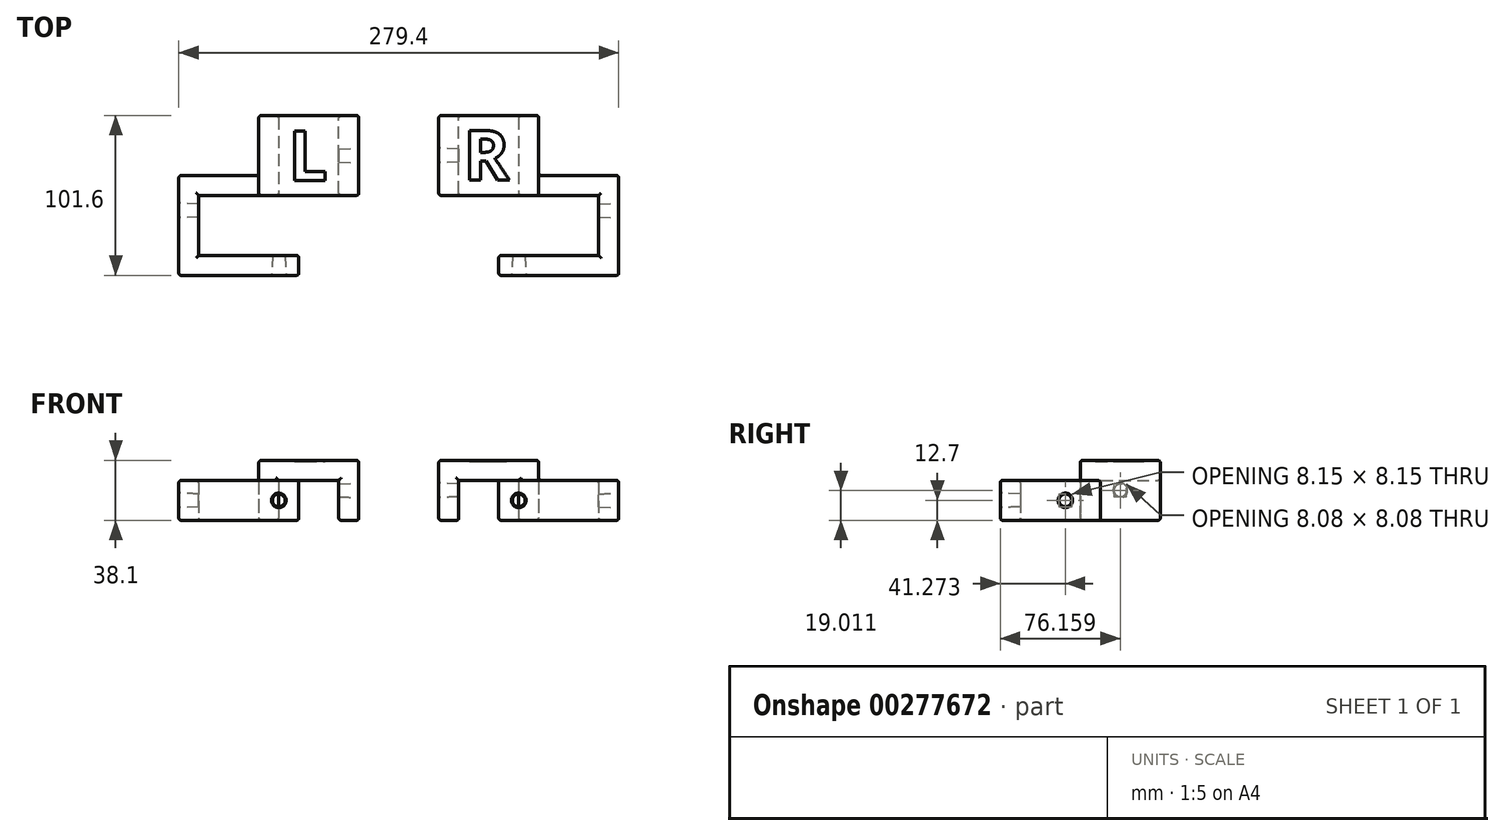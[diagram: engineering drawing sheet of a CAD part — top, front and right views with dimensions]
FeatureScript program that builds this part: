
annotation { "Feature Type Name" : "Feature", "Feature Type Description" : "" }
export const myFeature = defineFeature(function(context is Context, id is Id, definition is map)
    precondition{}
    {
        {
            var Q0;
            Q0=qCreatedBy(makeId("Top.planeOp"),FACE);
            var sketch = newSketch(context, id + "F0", { "sketchPlane" : qUnion([Q0])});
            skLineSegment(sketch, "E0.bottom", {"start": v(0.5, -16.27) * mm, "end": v(-75.7, -16.27) * mm});
            skLineSegment(sketch, "E0.top", {"start": v(0.5, -3.57) * mm, "end": v(-63, -3.57) * mm});
            skLineSegment(sketch, "E0.left", {"start": v(0.5, -16.27) * mm, "end": v(0.5, -3.57) * mm});
            skLineSegment(sketch, "E1", {"start": v(-75.7, -16.27) * mm, "end": v(-75.7, 47.23) * mm});
            skLineSegment(sketch, "E2", {"start": v(-75.7, 47.23) * mm, "end": v(-24.9, 47.23) * mm});
            skLineSegment(sketch, "E3", {"start": v(-24.9, 47.23) * mm, "end": v(-24.9, 85.33) * mm});
            skLineSegment(sketch, "E4", {"start": v(-24.9, 85.33) * mm, "end": v(-12.2, 85.33) * mm});
            skLineSegment(sketch, "E5", {"start": v(-12.2, 85.33) * mm, "end": v(-12.2, 34.53) * mm});
            skLineSegment(sketch, "E6", {"start": v(-12.2, 34.53) * mm, "end": v(-63, 34.53) * mm});
            skLineSegment(sketch, "E7", {"start": v(-63, 34.53) * mm, "end": v(-63, -3.57) * mm});
            skSolve(sketch);
        }
        {
            var Q0;
            Q0 = qSketchRegion(id + "F0", true);
            extrude(context, id + "F1", {"entities" : qUnion([Q0]), "depth" : 25.4 * mm});
        }
        {
            var Q0;
            Q0=makeQuery(id+"F1.opExtrude","CAP_FACE",FACE,{"disambiguationData":[OSD([sQuery(id+"F0.wireOp",EDGE,"E0.bottom"),sQuery(id+"F0.wireOp",EDGE,"E0.top"),sQuery(id+"F0.wireOp",EDGE,"E0.left"),sQuery(id+"F0.wireOp",EDGE,"E1"),sQuery(id+"F0.wireOp",EDGE,"E2"),sQuery(id+"F0.wireOp",EDGE,"E3"),sQuery(id+"F0.wireOp",EDGE,"E4"),sQuery(id+"F0.wireOp",EDGE,"E5"),sQuery(id+"F0.wireOp",EDGE,"E6"),sQuery(id+"F0.wireOp",EDGE,"E7")])],"isStart":false});
            var sketch = newSketch(context, id + "F2", { "sketchPlane" : qUnion([Q0])});
            skLineSegment(sketch, "E8.bottom", {"start": v(-24.9, 85.33) * mm, "end": v(38.6, 85.33) * mm});
            skLineSegment(sketch, "E8.top", {"start": v(-24.9, 34.53) * mm, "end": v(38.6, 34.53) * mm});
            skLineSegment(sketch, "E8.left", {"start": v(-24.9, 85.33) * mm, "end": v(-24.9, 34.53) * mm});
            skLineSegment(sketch, "E8.right", {"start": v(38.6, 85.33) * mm, "end": v(38.6, 34.53) * mm});
            skSolve(sketch);
        }
        {
            var Q0;
            Q0 = qSketchRegion(id + "F2", true);
            extrude(context, id + "F3", {"entities" : qUnion([Q0]), "operationType" : NewBodyOperationType.ADD, "depth" : 12.7 * mm});
        }
        {
            var Q0;
            Q0=makeQuery(id+"F3.opExtrude","CAP_FACE",FACE,{"disambiguationData":[OSD([sQuery(id+"F2.wireOp",EDGE,"E8.bottom"),sQuery(id+"F2.wireOp",EDGE,"E8.top"),sQuery(id+"F2.wireOp",EDGE,"E8.left"),sQuery(id+"F2.wireOp",EDGE,"E8.right")])],"isStart":true});
            var sketch = newSketch(context, id + "F4", { "sketchPlane" : qUnion([Q0])});
            skLineSegment(sketch, "E9.bottom", {"start": v(38.6, -34.53) * mm, "end": v(25.9, -34.53) * mm});
            skLineSegment(sketch, "E9.top", {"start": v(38.6, -85.33) * mm, "end": v(25.9, -85.33) * mm});
            skLineSegment(sketch, "E9.left", {"start": v(38.6, -34.53) * mm, "end": v(38.6, -85.33) * mm});
            skLineSegment(sketch, "E9.right", {"start": v(25.9, -34.53) * mm, "end": v(25.9, -85.33) * mm});
            skSolve(sketch);
        }
        {
            var Q0;
            Q0 = qSketchRegion(id + "F4", true);
            extrude(context, id + "F5", {"entities" : qUnion([Q0]), "operationType" : NewBodyOperationType.ADD, "depth" : 25.4 * mm});
        }
        {
            var Q0;
            Q0=makeQuery(id+"F1.opExtrude","SWEPT_FACE",FACE,{"disambiguationData":[OSD([sQuery(id+"F0.wireOp",EDGE,"E0.bottom")])]});
            var sketch = newSketch(context, id + "F6", { "sketchPlane" : qUnion([Q0])});
            skLineSegment(sketch, "E10", {"start": v(0.5, 12.7) * mm, "end": v(-12.2, 12.7) * mm, "construction": true});
            skCircle(sketch, "E11", {"center": v(-12.2, 12.7) * mm, "radius": 4.61 * mm});
            skSolve(sketch);
        }
        {
            var Q0;
            Q0=makeQuery(id+"F1.opExtrude","SWEPT_FACE",FACE,{"disambiguationData":[OSD([sQuery(id+"F0.wireOp",EDGE,"E0.top")])]});
            var sketch = newSketch(context, id + "F7", { "sketchPlane" : qUnion([Q0])});
            skPoint(sketch, "E12.0", {"position": v(12.2, 12.7) * mm});
            skCircle(sketch, "E13", {"center": v(12.2, 12.7) * mm, "radius": 4.08 * mm});
            skSolve(sketch);
        }
        {
            var Q0;
            Q0=makeQuery(id+"F1.opExtrude","SWEPT_FACE",FACE,{"disambiguationData":[OSD([sQuery(id+"F0.wireOp",EDGE,"E1")])]});
            var sketch = newSketch(context, id + "F8", { "sketchPlane" : qUnion([Q0])});
            skLineSegment(sketch, "E14", {"start": v(-47.23, 12.7) * mm, "end": v(-25, 12.7) * mm, "construction": true});
            skCircle(sketch, "E15", {"center": v(-25, 12.7) * mm, "radius": 4.61 * mm});
            skSolve(sketch);
        }
        {
            var Q0;
            Q0=makeQuery(id+"F1.opExtrude","SWEPT_FACE",FACE,{"disambiguationData":[OSD([sQuery(id+"F0.wireOp",EDGE,"E7")])]});
            var sketch = newSketch(context, id + "F9", { "sketchPlane" : qUnion([Q0])});
            skPoint(sketch, "E16.0", {"position": v(25, 12.7) * mm});
            skCircle(sketch, "E17", {"center": v(25, 12.7) * mm, "radius": 4.08 * mm});
            skSolve(sketch);
        }
        {
            var Q0;
            Q0=makeQuery(id+"F5.boolean.opBoolean","MERGE",FACE,{"derivedFrom":[makeQuery(id+"F3.opExtrude","SWEPT_FACE",FACE,{"disambiguationData":[OSD([sQuery(id+"F2.wireOp",EDGE,"E8.right")])]}),makeQuery(id+"F5.opExtrude","SWEPT_FACE",FACE,{"disambiguationData":[OSD([sQuery(id+"F4.wireOp",EDGE,"E9.left")])]})]});
            var sketch = newSketch(context, id + "F10", { "sketchPlane" : qUnion([Q0])});
            skLineSegment(sketch, "E18", {"start": v(34.53, 19.05) * mm, "end": v(59.93, 19.05) * mm, "construction": true});
            skLineSegment(sketch, "E19", {"start": v(59.93, 19.05) * mm, "end": v(59.93, 0) * mm, "construction": true});
            skCircle(sketch, "E20", {"center": v(59.93, 19.05) * mm, "radius": 4.61 * mm});
            skSolve(sketch);
        }
        {
            var Q0;
            Q0=makeQuery(id+"F5.opExtrude","SWEPT_FACE",FACE,{"disambiguationData":[OSD([sQuery(id+"F4.wireOp",EDGE,"E9.right")])]});
            var sketch = newSketch(context, id + "F11", { "sketchPlane" : qUnion([Q0])});
            skPoint(sketch, "E21.0", {"position": v(-59.93, 19.05) * mm});
            skCircle(sketch, "E22", {"center": v(-59.93, 19.05) * mm, "radius": 4.08 * mm});
            skSolve(sketch);
        }
        {
            var Q1;
            Q1=makeQuery(id+"F10.imprint","IMPRINT",FACE,{"disambiguationData":[TD([[makeQuery(id+"F10.imprint","IMPRINT",EDGE,{"derivedFrom":sQuery(id+"F10.wireOp",EDGE,"E20")}),1.0]])]});
            var Q2;
            Q2=makeQuery(id+"F11.imprint","IMPRINT",FACE,{"disambiguationData":[TD([[makeQuery(id+"F11.imprint","IMPRINT",EDGE,{"derivedFrom":sQuery(id+"F11.wireOp",EDGE,"E22")}),1.0]])]});
            loft(context, id + "F12", {"operationType" : NewBodyOperationType.REMOVE, "sheetProfilesArray" : [{ "sheetProfileEntities" : qUnion([Q1]) }, { "sheetProfileEntities" : qUnion([Q2]) }]});
        }
        {
            var Q1;
            Q1=makeQuery(id+"F6.imprint","IMPRINT",FACE,{"disambiguationData":[TD([[makeQuery(id+"F6.imprint","IMPRINT",EDGE,{"derivedFrom":sQuery(id+"F6.wireOp",EDGE,"E11")}),1.0]])]});
            var Q2;
            Q2=makeQuery(id+"F7.imprint","IMPRINT",FACE,{"disambiguationData":[TD([[makeQuery(id+"F7.imprint","IMPRINT",EDGE,{"derivedFrom":sQuery(id+"F7.wireOp",EDGE,"E13")}),1.0]])]});
            loft(context, id + "F13", {"operationType" : NewBodyOperationType.REMOVE, "sheetProfilesArray" : [{ "sheetProfileEntities" : qUnion([Q1]) }, { "sheetProfileEntities" : qUnion([Q2]) }]});
        }
        {
            var Q1;
            Q1=makeQuery(id+"F8.imprint","IMPRINT",FACE,{"disambiguationData":[TD([[makeQuery(id+"F8.imprint","IMPRINT",EDGE,{"derivedFrom":sQuery(id+"F8.wireOp",EDGE,"E15")}),1.0]])]});
            var Q2;
            Q2=makeQuery(id+"F9.imprint","IMPRINT",FACE,{"disambiguationData":[TD([[makeQuery(id+"F9.imprint","IMPRINT",EDGE,{"derivedFrom":sQuery(id+"F9.wireOp",EDGE,"E17")}),1.0]])]});
            loft(context, id + "F14", {"operationType" : NewBodyOperationType.REMOVE, "sheetProfilesArray" : [{ "sheetProfileEntities" : qUnion([Q1]) }, { "sheetProfileEntities" : qUnion([Q2]) }]});
        }
        {
            var Q0;
            Q0=makeQuery(id+"F1.opExtrude","CAP_FACE",FACE,{"disambiguationData":[OSD([sQuery(id+"F0.wireOp",EDGE,"E0.bottom"),sQuery(id+"F0.wireOp",EDGE,"E0.top"),sQuery(id+"F0.wireOp",EDGE,"E0.left"),sQuery(id+"F0.wireOp",EDGE,"E1"),sQuery(id+"F0.wireOp",EDGE,"E2"),sQuery(id+"F0.wireOp",EDGE,"E3"),sQuery(id+"F0.wireOp",EDGE,"E4"),sQuery(id+"F0.wireOp",EDGE,"E5"),sQuery(id+"F0.wireOp",EDGE,"E6"),sQuery(id+"F0.wireOp",EDGE,"E7")])],"isStart":false});
            var Q1;
            Q1=makeQuery(id+"F1.opExtrude","CAP_FACE",FACE,{"disambiguationData":[OSD([sQuery(id+"F0.wireOp",EDGE,"E0.bottom"),sQuery(id+"F0.wireOp",EDGE,"E0.top"),sQuery(id+"F0.wireOp",EDGE,"E0.left"),sQuery(id+"F0.wireOp",EDGE,"E1"),sQuery(id+"F0.wireOp",EDGE,"E2"),sQuery(id+"F0.wireOp",EDGE,"E3"),sQuery(id+"F0.wireOp",EDGE,"E4"),sQuery(id+"F0.wireOp",EDGE,"E5"),sQuery(id+"F0.wireOp",EDGE,"E6"),sQuery(id+"F0.wireOp",EDGE,"E7")])],"isStart":true});
            var Q2;
            Q2=makeQuery(id+"F5.opExtrude","CAP_FACE",FACE,{"disambiguationData":[OSD([sQuery(id+"F4.wireOp",EDGE,"E9.bottom"),sQuery(id+"F4.wireOp",EDGE,"E9.top"),sQuery(id+"F4.wireOp",EDGE,"E9.left"),sQuery(id+"F4.wireOp",EDGE,"E9.right")])],"isStart":false});
            var Q3;
            Q3=makeQuery(id+"F5.boolean.opBoolean","MERGE",FACE,{"derivedFrom":[makeQuery(id+"F3.boolean.opBoolean","MERGE",FACE,{"derivedFrom":[makeQuery(id+"F1.opExtrude","SWEPT_FACE",FACE,{"disambiguationData":[OSD([sQuery(id+"F0.wireOp",EDGE,"E4")])]}),makeQuery(id+"F3.opExtrude","SWEPT_FACE",FACE,{"disambiguationData":[OSD([sQuery(id+"F2.wireOp",EDGE,"E8.bottom")])]})]}),makeQuery(id+"F5.opExtrude","SWEPT_FACE",FACE,{"disambiguationData":[OSD([sQuery(id+"F4.wireOp",EDGE,"E9.top")])]})]});
            var Q4;
            Q4=makeQuery(id+"F3.boolean.opBoolean","MERGE",FACE,{"derivedFrom":[makeQuery(id+"F1.opExtrude","SWEPT_FACE",FACE,{"disambiguationData":[OSD([sQuery(id+"F0.wireOp",EDGE,"E3")])]}),makeQuery(id+"F3.opExtrude","SWEPT_FACE",FACE,{"disambiguationData":[OSD([sQuery(id+"F2.wireOp",EDGE,"E8.left")])]})]});
            var Q5;
            Q5=makeQuery(id+"F3.opExtrude","CAP_FACE",FACE,{"disambiguationData":[OSD([sQuery(id+"F2.wireOp",EDGE,"E8.bottom"),sQuery(id+"F2.wireOp",EDGE,"E8.top"),sQuery(id+"F2.wireOp",EDGE,"E8.left"),sQuery(id+"F2.wireOp",EDGE,"E8.right")])],"isStart":false});
            var Q6;
            Q6=makeQuery(id+"F1.opExtrude","SWEPT_FACE",FACE,{"disambiguationData":[OSD([sQuery(id+"F0.wireOp",EDGE,"E0.left")])]});
            var Q7;
            Q7=makeQuery(id+"F5.boolean.opBoolean","MERGE",EDGE,{"derivedFrom":[makeQuery(id+"F3.opExtrude","SWEPT_EDGE",EDGE,{"disambiguationData":[OSD([sQuery(id+"F2.wireOp",EDGE,"E8.top"),sQuery(id+"F2.wireOp",EDGE,"E8.right")])]}),makeQuery(id+"F5.opExtrude","SWEPT_EDGE",EDGE,{"disambiguationData":[OSD([sQuery(id+"F4.wireOp",EDGE,"E9.bottom"),sQuery(id+"F4.wireOp",EDGE,"E9.left")])]})]});
            var Q8;
            Q8=makeQuery(id+"F5.opExtrude","SWEPT_EDGE",EDGE,{"disambiguationData":[OSD([sQuery(id+"F2.wireOp",EDGE,"E8.top"),sQuery(id+"F4.wireOp",EDGE,"E9.bottom"),sQuery(id+"F4.wireOp",EDGE,"E9.right")])]});
            var Q9;
            Q9=makeQuery(id+"F3.opExtrude","CAP_EDGE",EDGE,{"disambiguationData":[OSD([sQuery(id+"F2.wireOp",EDGE,"E8.top")])],"isStart":true});
            var Q10;
            Q10=makeQuery(id+"F1.opExtrude","SWEPT_EDGE",EDGE,{"disambiguationData":[OSD([sQuery(id+"F0.wireOp",EDGE,"E5"),sQuery(id+"F0.wireOp",EDGE,"E6")])]});
            var Q11;
            Q11=makeQuery(id+"F1.opExtrude","SWEPT_EDGE",EDGE,{"disambiguationData":[OSD([sQuery(id+"F0.wireOp",EDGE,"E0.bottom"),sQuery(id+"F0.wireOp",EDGE,"E1")])]});
            var Q12;
            Q12=makeQuery(id+"F1.opExtrude","SWEPT_EDGE",EDGE,{"disambiguationData":[OSD([sQuery(id+"F0.wireOp",EDGE,"E1"),sQuery(id+"F0.wireOp",EDGE,"E2")])]});
            fillet(context, id + "F15", {"entities" : qUnion([Q0, Q1, Q2, Q3, Q4, Q5, Q6, Q7, Q8, Q9, Q10, Q11, Q12]), "radius" : 1.59 * mm, "tangentPropagation" : true, "allowEdgeOverflow" : false});
        }
        {
            var Q0;
            Q0=makeQuery(id+"F5.boolean.opBoolean","MERGE",FACE,{"derivedFrom":[makeQuery(id+"F3.opExtrude","SWEPT_FACE",FACE,{"disambiguationData":[OSD([sQuery(id+"F2.wireOp",EDGE,"E8.right")])]}),makeQuery(id+"F5.opExtrude","SWEPT_FACE",FACE,{"disambiguationData":[OSD([sQuery(id+"F4.wireOp",EDGE,"E9.left")])]})]});
            cPlane(context, id + "F16", {"entities" : qUnion([Q0]), "cplaneType" : CPlaneType.OFFSET, "offset" : 25.4 * mm, "width" : 152.4 * mm, "height" : 152.4 * mm});
        }
        {
            var Q0;
            Q0=makeQuery(id+"F1.opExtrude","SWEPT_BODY",BODY,{"disambiguationData":[OSD([sQuery(id+"F0.wireOp",EDGE,"E0.bottom"),sQuery(id+"F0.wireOp",EDGE,"E0.top"),sQuery(id+"F0.wireOp",EDGE,"E0.left"),sQuery(id+"F0.wireOp",EDGE,"E1"),sQuery(id+"F0.wireOp",EDGE,"E2"),sQuery(id+"F0.wireOp",EDGE,"E3"),sQuery(id+"F0.wireOp",EDGE,"E4"),sQuery(id+"F0.wireOp",EDGE,"E5"),sQuery(id+"F0.wireOp",EDGE,"E6"),sQuery(id+"F0.wireOp",EDGE,"E7")])]});
            var Q1;
            Q1=qCreatedBy(id+"F16.planeOp",FACE);
            mirror(context, id + "F17", {"entities" : qUnion([Q0]), "mirrorPlane" : qUnion([Q1])});
        }
        {
            var Q0;
            Q0=makeQuery(id+"F3.opExtrude","CAP_FACE",FACE,{"disambiguationData":[OSD([sQuery(id+"F2.wireOp",EDGE,"E8.bottom"),sQuery(id+"F2.wireOp",EDGE,"E8.top"),sQuery(id+"F2.wireOp",EDGE,"E8.left"),sQuery(id+"F2.wireOp",EDGE,"E8.right")])],"isStart":false});
            var sketch = newSketch(context, id + "F18", { "sketchPlane" : qUnion([Q0])});
            skText(sketch, "E23", { "text": "L", "fontName": "OpenSans-Bold.ttf"});
            skPoint(sketch, "E24", {"position": v(6.85, 83.74) * mm});
            skLineSegment(sketch, "E25", {"start": v(-23.3, 59.93) * mm, "end": v(-6.28, 59.93) * mm, "construction": true});
            skLineSegment(sketch, "E26", {"start": v(6.85, 83.74) * mm, "end": v(6.85, 75.8) * mm, "construction": true});
            const initialGuessF18  = {"E23": [-0.00628, 0.04405, 1, 0, 0.03175]};
            skSetInitialGuess(sketch, initialGuessF18);
            skSolve(sketch);
        }
        {
            var Q0;
            Q0=makeQuery(id+"F17.opPattern","COPY",FACE,{"derivedFrom":makeQuery(id+"F3.opExtrude","CAP_FACE",FACE,{"disambiguationData":[OSD([sQuery(id+"F2.wireOp",EDGE,"E8.bottom"),sQuery(id+"F2.wireOp",EDGE,"E8.top"),sQuery(id+"F2.wireOp",EDGE,"E8.left"),sQuery(id+"F2.wireOp",EDGE,"E8.right")])],"isStart":false}),"instanceName":"1"});
            var sketch = newSketch(context, id + "F19", { "sketchPlane" : qUnion([Q0])});
            skText(sketch, "E27", { "text": "R", "fontName": "OpenSans-Bold.ttf"});
            skLineSegment(sketch, "E28", {"start": v(121.15, 83.74) * mm, "end": v(121.15, 76.12) * mm, "construction": true});
            skLineSegment(sketch, "E29", {"start": v(91, 59.93) * mm, "end": v(105.17, 59.93) * mm, "construction": true});
            const initialGuessF19  = {"E27": [0.10517, 0.04437, 1, 0, 0.03175]};
            skSetInitialGuess(sketch, initialGuessF19);
            skSolve(sketch);
        }
        {
            var Q0;
            Q0 = qSketchRegion(id + "F18", true);
            var Q1;
            Q1 = qSketchRegion(id + "F19", true);
            extrude(context, id + "F20", {"entities" : qUnion([Q0, Q1]), "operationType" : NewBodyOperationType.REMOVE, "oppositeDirection" : true, "depth" : 0.8 * mm});
        }
    });
